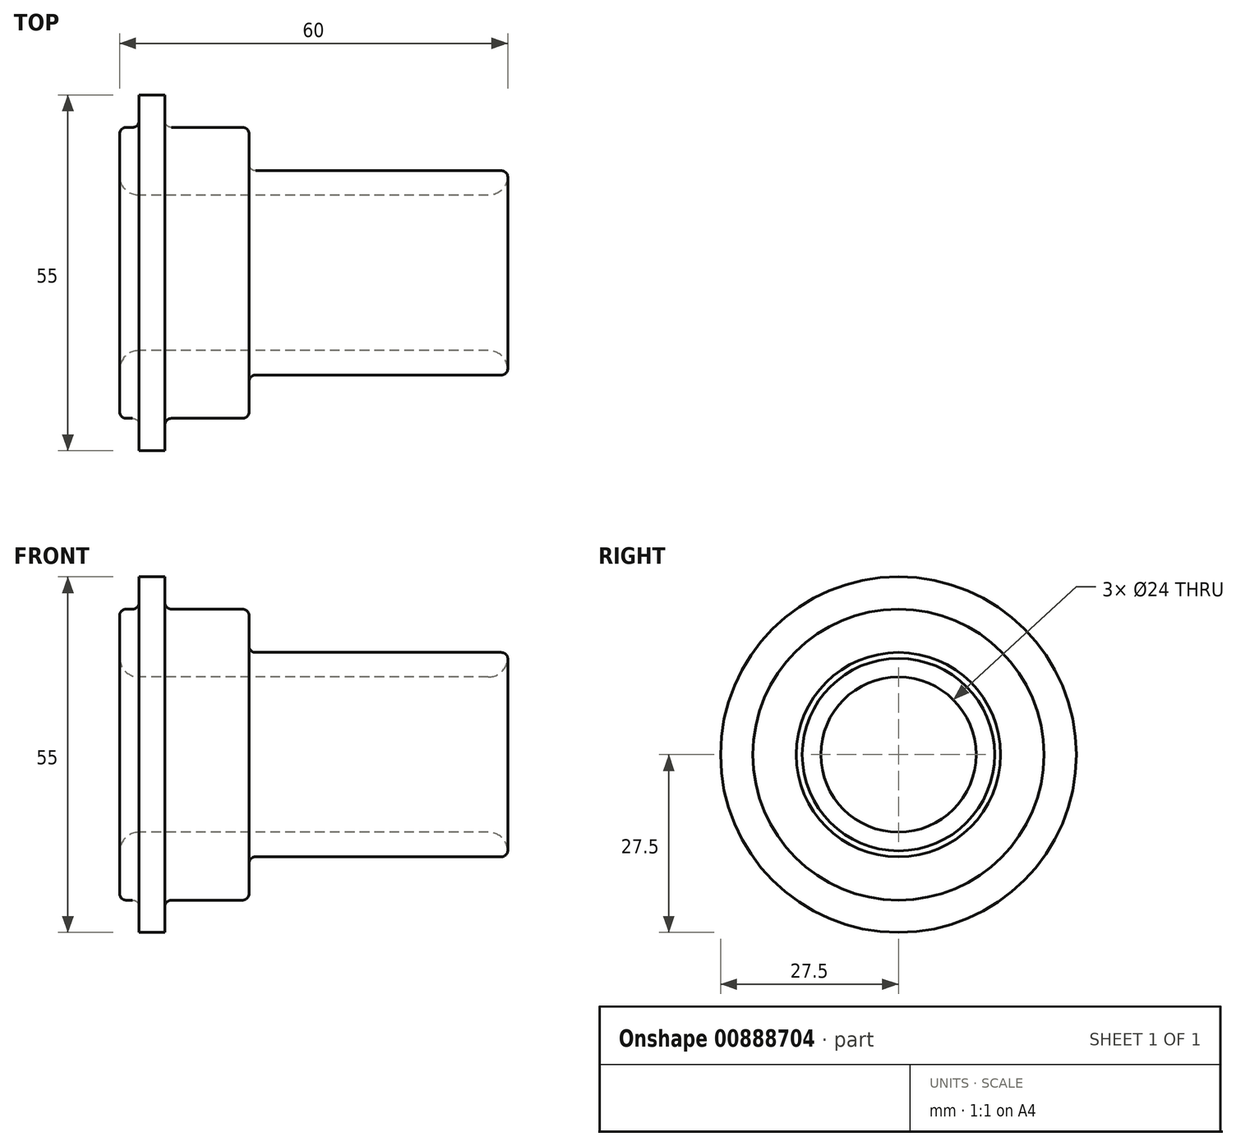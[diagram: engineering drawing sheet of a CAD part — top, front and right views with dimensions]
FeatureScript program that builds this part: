
annotation { "Feature Type Name" : "Feature", "Feature Type Description" : "" }
export const myFeature = defineFeature(function(context is Context, id is Id, definition is map)
    precondition{}
    {
        {
            var Q0;
            Q0=qCreatedBy(makeId("Front.planeOp"),FACE);
            var sketch = newSketch(context, id + "F0", { "sketchPlane" : qUnion([Q0])});
            skLineSegment(sketch, "E0", {"start": v(-40.71, 0) * mm, "end": v(36.59, 0) * mm});
            skLineSegment(sketch, "E1", {"start": v(-39.62, 15) * mm, "end": v(-39.62, 21.5) * mm});
            skLineSegment(sketch, "E2", {"start": v(-38.62, 22.5) * mm, "end": v(-37.62, 22.5) * mm});
            skLineSegment(sketch, "E3", {"start": v(-36.62, 23.5) * mm, "end": v(-36.62, 27.5) * mm});
            skLineSegment(sketch, "E4", {"start": v(-36.62, 27.5) * mm, "end": v(-32.62, 27.5) * mm});
            skLineSegment(sketch, "E5", {"start": v(-32.62, 27.5) * mm, "end": v(-32.62, 23.5) * mm});
            skLineSegment(sketch, "E6", {"start": v(-31.62, 22.5) * mm, "end": v(-20.62, 22.5) * mm});
            skLineSegment(sketch, "E7", {"start": v(-19.62, 21.5) * mm, "end": v(-19.62, 16.8) * mm});
            skLineSegment(sketch, "E8", {"start": v(-18.62, 15.8) * mm, "end": v(19.38, 15.8) * mm});
            skLineSegment(sketch, "E9", {"start": v(20.38, 15) * mm, "end": v(20.38, 14.8) * mm});
            skLineSegment(sketch, "E10", {"start": v(17.38, 12) * mm, "end": v(-36.62, 12) * mm});
            skPoint(sketch, "E11.visualSharp", {"position": v(-39.62, 22.5) * mm});
            skArc(sketch, "E11.filletArc", {"start": v(-38.62, 22.5) * mm, "mid": v(-39.33, 22.2) * mm, "end": v(-39.62, 21.5) * mm});
            skPoint(sketch, "E12.visualSharp", {"position": v(-36.62, 22.5) * mm});
            skArc(sketch, "E12.filletArc", {"start": v(-37.62, 22.5) * mm, "mid": v(-36.92, 22.8) * mm, "end": v(-36.62, 23.5) * mm});
            skPoint(sketch, "E13.visualSharp", {"position": v(-32.62, 22.5) * mm});
            skArc(sketch, "E13.filletArc", {"start": v(-32.62, 23.5) * mm, "mid": v(-32.33, 22.8) * mm, "end": v(-31.62, 22.5) * mm});
            skPoint(sketch, "E14.visualSharp", {"position": v(-19.62, 22.5) * mm});
            skArc(sketch, "E14.filletArc", {"start": v(-19.62, 21.5) * mm, "mid": v(-19.92, 22.2) * mm, "end": v(-20.62, 22.5) * mm});
            skPoint(sketch, "E15.visualSharp", {"position": v(-19.62, 15.8) * mm});
            skArc(sketch, "E15.filletArc", {"start": v(-19.62, 16.8) * mm, "mid": v(-19.33, 16.1) * mm, "end": v(-18.62, 15.8) * mm});
            skPoint(sketch, "E16.visualSharp", {"position": v(20.38, 15.8) * mm});
            skArc(sketch, "E16.filletArc", {"start": v(20.38, 14.8) * mm, "mid": v(20.08, 15.5) * mm, "end": v(19.38, 15.8) * mm});
            skPoint(sketch, "E17.visualSharp", {"position": v(-39.62, 12) * mm});
            skArc(sketch, "E17.filletArc", {"start": v(-39.62, 15) * mm, "mid": v(-38.74, 12.88) * mm, "end": v(-36.62, 12) * mm});
            skPoint(sketch, "E18.visualSharp", {"position": v(20.38, 12) * mm});
            skArc(sketch, "E18.filletArc", {"start": v(17.38, 12) * mm, "mid": v(19.5, 12.88) * mm, "end": v(20.38, 15) * mm});
            skSolve(sketch);
        }
        {
            var Q0;
            Q0 = qSketchRegion(id + "F0", true);
            var Q1;
            Q1=sQuery(id+"F0.wireOp",EDGE,"E0");
            revolve(context, id + "F1", {"surfaceOperationType" : NewSurfaceOperationType.NEW, "entities" : qUnion([Q0]), "axis" : qUnion([Q1]), "revolveType" : RevolveType.FULL});
        }
        {
            var Q0;
            Q0=makeQuery(id+"F1.opRevolve","SWEPT_BODY",BODY,{"disambiguationData":[OSD([sQuery(id+"F0.wireOp",EDGE,"E9"),sQuery(id+"F0.wireOp",EDGE,"E16.filletArc"),sQuery(id+"F0.wireOp",EDGE,"E18.filletArc")])]});
            deleteBodies(context, id + "F2", {"entities" : qUnion([Q0])});
        }
    });
